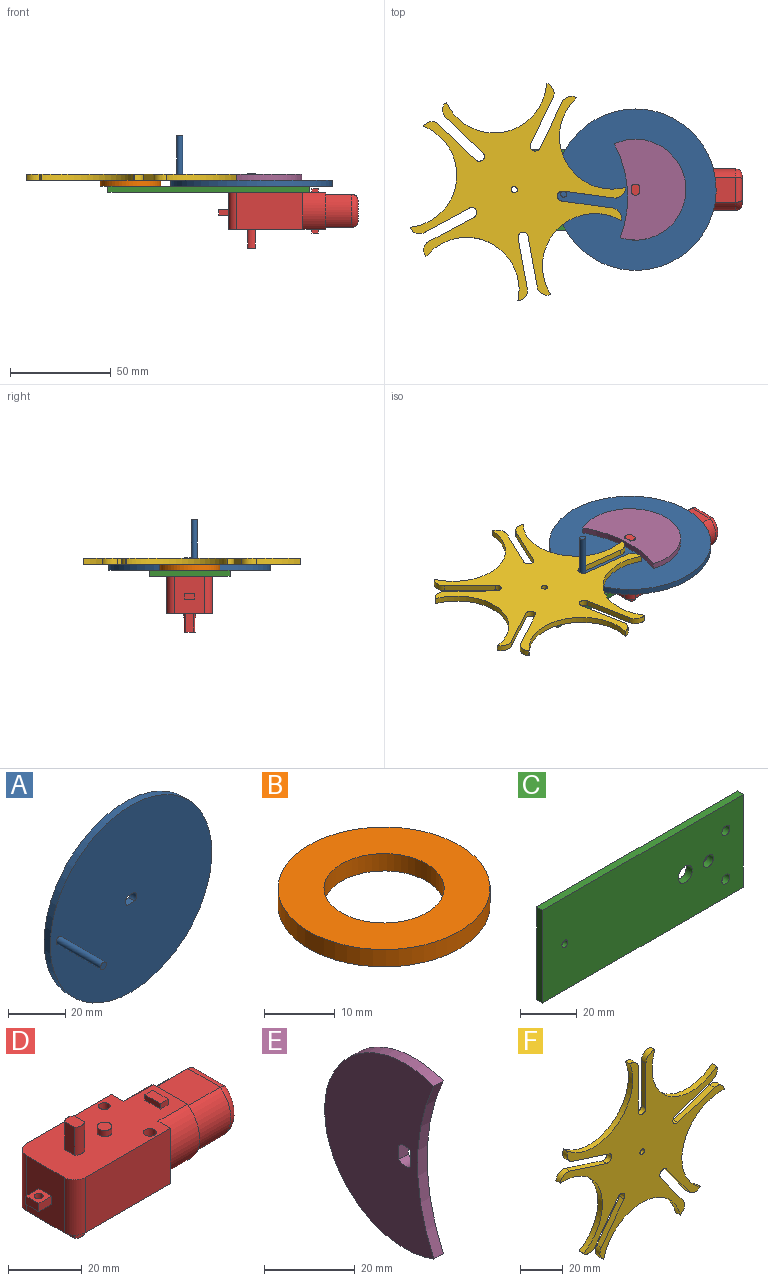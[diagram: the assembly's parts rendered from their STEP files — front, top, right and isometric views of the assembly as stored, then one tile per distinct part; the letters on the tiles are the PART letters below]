
ASSEMBLY  parts=6 mates=5
PART A: 9 faces, bbox 80x25x80 mm
  f0: cylinder r=2.7mm len=3.8mm, axis (0,1,0), area 12.6mm2, adj f1,f4,f5,f6
  f1: plane 3.84x3mm, normal (0,0,-1), area 11.5mm2, adj f0,f2,f5,f6
  f2: cylinder r=2.7mm len=3.8mm, axis (0,1,0), area 12.6mm2, adj f1,f4,f5,f6
  f3: cylinder r=40mm len=80mm, axis (0,1,0), area 754mm2, adj f5,f6
  f4: plane 3.84x3mm, normal (0,0,1), area 11.5mm2, adj f0,f2,f5,f6
  f5: plane 80x80mm, normal (0,-1,0), area 5000.8mm2, adj f0,f1,f2,f3,f4,f7
  f6: plane 80x80mm, normal (0,1,0), area 5007.9mm2, adj f0,f1,f2,f3,f4
  f7: cylinder r=1.5mm len=22mm, axis (0,1,0), area 207.3mm2, adj f5,f8
  f8: plane 3x3mm, normal (0,-1,0), area 7.1mm2, adj f7
PART B: 4 faces, bbox 30x30x3 mm
  f0: cylinder r=8.5mm len=17mm, axis (0,0,-1), area 160.2mm2, adj f2,f3
  f1: cylinder r=15mm len=30mm, axis (0,0,-1), area 282.7mm2, adj f2,f3
  f2: plane 30x30mm, normal (0,0,1), area 479.9mm2, adj f0,f1
  f3: plane 30x30mm, normal (0,0,-1), area 479.9mm2, adj f0,f1
PART C: 11 faces, bbox 100x3x40 mm
  f0: plane 100x3mm, normal (0,0,1), area 300mm2, adj f1,f8,f9,f10
  f1: plane 40x3mm, normal (-1,0,0), area 120mm2, adj f0,f2,f9,f10
  f2: plane 100x3mm, normal (0,0,-1), area 300mm2, adj f1,f8,f9,f10
  f3: cylinder r=1.5mm len=3mm, axis (0,1,0), area 28.3mm2, adj f9,f10
  f4: cylinder r=3.5mm len=7mm, axis (0,1,0), area 66mm2, adj f9,f10
  f5: cylinder r=2.5mm len=5mm, axis (0,1,0), area 47.1mm2, adj f9,f10
  f6: cylinder r=2mm len=4mm, axis (0,1,0), area 37.7mm2, adj f9,f10
  f7: cylinder r=2mm len=4mm, axis (0,1,0), area 37.7mm2, adj f9,f10
  f8: plane 40x3mm, normal (1,0,0), area 120mm2, adj f0,f2,f9,f10
  f9: plane 100x40mm, normal (0,-1,0), area 3909.7mm2, adj f0,f1,f2,f3,f4,f5,f6,f7
  f10: plane 100x40mm, normal (0,1,0), area 3909.7mm2, adj f0,f1,f2,f3,f4,f5,f6,f7
PART D: 53 faces, bbox 69.1x22.6x37 mm
  f0: plane 22.6x18.4mm, normal (1,0,0), area 66.1mm2, adj f8,f9,f17,f18,f19,f20,f21,f22
  f1: plane 9.2x4.74mm, normal (1,0,0), area 13mm2, adj f5,f8,f17
  f2: plane 9.2x4.74mm, normal (1,0,0), area 13mm2, adj f5,f9,f17
  f3: plane 9.2x4.74mm, normal (1,0,0), area 13mm2, adj f7,f9,f18
  f4: plane 18.4x14.6mm, normal (-1,0,0), area 255.1mm2, adj f8,f9,f10,f11,f12,f14,f16,f40
  f5: plane 32.8x18.4mm, normal (0,-1,0), area 603.5mm2, adj f1,f2,f8,f9,f10
  f6: plane 9.2x4.74mm, normal (1,0,0), area 13mm2, adj f7,f8,f18
  f7: plane 32.8x18.4mm, normal (0,1,0), area 603.5mm2, adj f3,f6,f8,f9,f11
  f8: plane 48.1x22.6mm, normal (0,0,1), area 906.1mm2, adj f0,f1,f4,f5,f6,f7,f10,f11
  f9: plane 48.1x22.6mm, normal (0,0,-1), area 918.6mm2, adj f0,f2,f3,f4,f5,f7,f10,f11
  f10: cylinder r=4mm len=18.4mm, axis (0,0,1), area 115.6mm2, adj f4,f5,f8,f9
  f11: cylinder r=4mm len=18.4mm, axis (0,0,-1), area 115.6mm2, adj f4,f7,f8,f9
  f12: plane 5x2.7mm, normal (0,1,0), area 13.5mm2, adj f4,f13,f16,f40
  f13: plane 5x2.7mm, normal (-1,0,0), area 13.5mm2, adj f12,f14,f16,f40
  f14: plane 5x2.7mm, normal (0,-1,0), area 13.5mm2, adj f4,f13,f16,f40
  f15: cylinder r=1.25mm len=2.7mm, axis (0,0,-1), area 21.2mm2, adj f16,f40
  f16: plane 5x5mm, normal (0,0,1), area 20.1mm2, adj f4,f12,f13,f14,f15
  f17: cylinder r=11.3mm len=18.4mm, axis (-1,0,0), area 242.9mm2, adj f0,f1,f2,f8,f9
  f18: cylinder r=11.3mm len=18.4mm, axis (-1,0,0), area 242.9mm2, adj f0,f3,f6,f8,f9
  f19: plane 13x12.47mm, normal (0,0,1), area 162.1mm2, adj f0,f20,f22,f34
  f20: cylinder r=10.3mm len=16.4mm, axis (-1,0,0), area 246.6mm2, adj f0,f19,f21,f36
  f21: plane 13x12.47mm, normal (0,0,-1), area 162.1mm2, adj f0,f20,f22,f37
  f22: cylinder r=10.3mm len=16.4mm, axis (-1,0,0), area 246.6mm2, adj f0,f19,f21,f35
  f23: plane 14.6x10.4mm, normal (1,0,0), area 137.8mm2, adj f34,f35,f36,f37
  f24: plane 5.4x3.75mm, normal (0,0,-1), area 18.5mm2, adj f25,f26,f27,f28
  f25: cylinder r=2.7mm len=9.3mm, axis (0,0,-1), area 38.6mm2, adj f9,f24,f26,f28
  f26: plane 9.3x3.89mm, normal (-1,0,0), area 36.1mm2, adj f9,f24,f25,f27
  f27: cylinder r=2.7mm len=9.3mm, axis (0,0,-1), area 38.6mm2, adj f9,f24,f26,f28
  f28: plane 9.3x3.89mm, normal (1,0,0), area 36.1mm2, adj f9,f24,f25,f27
  f29: plane 9.3x3.89mm, normal (1,0,0), area 36.1mm2, adj f8,f30,f32,f33
  f30: cylinder r=2.7mm len=9.3mm, axis (0,0,-1), area 38.6mm2, adj f8,f29,f31,f33
  f31: plane 9.3x3.89mm, normal (-1,0,0), area 36.1mm2, adj f8,f30,f32,f33
  f32: cylinder r=2.7mm len=9.3mm, axis (0,0,-1), area 38.6mm2, adj f8,f29,f31,f33
  f33: plane 5.4x3.75mm, normal (0,0,1), area 18.5mm2, adj f29,f30,f31,f32
  f34: cylinder r=3mm len=12.47mm, axis (0,1,0), area 55.1mm2, adj f19,f23,f35,f36
  f35: torus R=7.3mm, axis (1,0,0), area 76.6mm2, adj f22,f23,f34,f37
  f36: torus R=7.3mm, axis (1,0,0), area 76.6mm2, adj f20,f23,f34,f37
  f37: cylinder r=3mm len=12.47mm, axis (0,-1,0), area 55.1mm2, adj f21,f23,f35,f36
  f38: cylinder r=2mm len=4mm, axis (0,0,-1), area 25.1mm2, adj f8,f39
  f39: plane 4x4mm, normal (0,0,1), area 12.6mm2, adj f38
  f40: plane 5x5mm, normal (0,0,-1), area 20.1mm2, adj f4,f12,f13,f14,f15
  f41: cylinder r=1.78mm len=18.4mm, axis (0,0,1), area 205.7mm2, adj f8,f9
  f42: cylinder r=1.6mm len=18.4mm, axis (0,0,1), area 185mm2, adj f8,f9
  f43: plane 6x3mm, normal (0,0,-1), area 18mm2, adj f44,f45,f46,f47
  f44: plane 6x1.8mm, normal (1,0,0), area 10.8mm2, adj f9,f43,f45,f47
  f45: plane 3x1.8mm, normal (0,-1,0), area 5.4mm2, adj f9,f43,f44,f46
  f46: plane 6x1.8mm, normal (-1,0,0), area 10.8mm2, adj f9,f43,f45,f47
  f47: plane 3x1.8mm, normal (0,1,0), area 5.4mm2, adj f9,f43,f44,f46
  f48: plane 3x1.8mm, normal (0,1,0), area 5.4mm2, adj f8,f49,f51,f52
  f49: plane 6x1.8mm, normal (-1,0,0), area 10.8mm2, adj f8,f48,f50,f52
  f50: plane 3x1.8mm, normal (0,-1,0), area 5.4mm2, adj f8,f49,f51,f52
  f51: plane 6x1.8mm, normal (1,0,0), area 10.8mm2, adj f8,f48,f50,f52
  f52: plane 6x3mm, normal (0,0,1), area 18mm2, adj f48,f49,f50,f51
PART E: 8 faces, bbox 3x34x50 mm
  f0: cylinder r=56.04mm len=46.62mm, axis (-1,0,0), area 144.2mm2, adj f5,f6,f7
  f1: cylinder r=2.7mm len=3.8mm, axis (-1,0,0), area 12.6mm2, adj f2,f4,f6,f7
  f2: plane 3.84x3mm, normal (0,1,0), area 11.5mm2, adj f1,f3,f6,f7
  f3: cylinder r=2.7mm len=3.8mm, axis (-1,0,0), area 12.6mm2, adj f2,f4,f6,f7
  f4: plane 3.84x3mm, normal (0,-1,0), area 11.5mm2, adj f1,f3,f6,f7
  f5: cylinder r=25mm len=50mm, axis (-1,0,0), area 291.1mm2, adj f0,f6,f7
  f6: plane 50x34.03mm, normal (1,0,0), area 1245.4mm2, adj f0,f1,f2,f3,f4,f5
  f7: plane 50x34.03mm, normal (-1,0,0), area 1245.4mm2, adj f0,f1,f2,f3,f4,f5
PART F: 43 faces, bbox 108.5x3x103.4 mm
  f0: plane 3x0.1mm, normal (-0.51,0,-0.86), area 0.3mm2, adj f1,f39,f41,f42
  f1: cylinder r=26mm len=50.53mm, axis (0,1,0), area 207.8mm2, adj f0,f2,f41,f42
  f2: cylinder r=55mm len=3mm, axis (0,1,0), area 0.6mm2, adj f1,f3,f41,f42
  f3: cylinder r=5mm len=7.38mm, axis (0,1,0), area 25.8mm2, adj f2,f4,f41,f42
  f4: plane 20.58x14.95mm, normal (0.81,0,0.59), area 76.3mm2, adj f3,f5,f41,f42
  f5: cylinder r=2.5mm len=4.52mm, axis (0,1,0), area 23.6mm2, adj f4,f6,f41,f42
  f6: plane 20.58x14.95mm, normal (-0.81,0,-0.59), area 76.3mm2, adj f5,f7,f41,f42
  f7: cylinder r=5mm len=7.36mm, axis (0,1,0), area 25mm2, adj f6,f8,f41,f42
  f8: plane 3x0.09mm, normal (0.66,0,-0.75), area 0.3mm2, adj f7,f9,f41,f42
  f9: cylinder r=26mm len=48.08mm, axis (0,1,0), area 207.8mm2, adj f8,f10,f41,f42
  f10: cylinder r=55mm len=3mm, axis (0,1,0), area 0.6mm2, adj f9,f11,f41,f42
  f11: cylinder r=5mm len=6.48mm, axis (0,1,0), area 25.8mm2, adj f10,f12,f41,f42
  f12: plane 24.19x7.86mm, normal (-0.31,0,0.95), area 76.3mm2, adj f11,f13,f41,f42
  f13: cylinder r=2.5mm len=4.88mm, axis (0,1,0), area 23.6mm2, adj f12,f14,f41,f42
  f14: plane 24.19x7.86mm, normal (0.31,0,-0.95), area 76.3mm2, adj f13,f15,f41,f42
  f15: cylinder r=5mm len=6.75mm, axis (0,1,0), area 25mm2, adj f14,f16,f41,f42
  f16: plane 3x0.11mm, normal (0.92,0,0.4), area 0.3mm2, adj f15,f17,f41,f42
  f17: cylinder r=26mm len=42.76mm, axis (0,1,0), area 207.8mm2, adj f16,f18,f41,f42
  f18: cylinder r=55mm len=3mm, axis (0,1,0), area 0.6mm2, adj f17,f19,f41,f42
  f19: cylinder r=5mm len=5.75mm, axis (0,1,0), area 25.8mm2, adj f18,f20,f41,f42
  f20: plane 25.43x3mm, normal (-1,0,0), area 76.3mm2, adj f19,f21,f41,f42
  f21: cylinder r=2.5mm len=5mm, axis (0,1,0), area 23.6mm2, adj f20,f22,f41,f42
  f22: plane 25.44x3mm, normal (1,0,0), area 76.3mm2, adj f21,f23,f41,f42
  f23: cylinder r=5mm len=5.48mm, axis (0,1,0), area 25mm2, adj f22,f24,f41,f42
  f24: plane 3x0.12mm, normal (-0.1,0,1), area 0.3mm2, adj f23,f25,f41,f42
  f25: cylinder r=26mm len=42.89mm, axis (0,1,0), area 207.8mm2, adj f24,f26,f41,f42
  f26: cylinder r=55mm len=3mm, axis (0,1,0), area 0.6mm2, adj f25,f27,f41,f42
  f27: cylinder r=5mm len=7mm, axis (0,1,0), area 25.8mm2, adj f26,f28,f41,f42
  f28: plane 24.19x7.86mm, normal (-0.31,0,-0.95), area 76.3mm2, adj f27,f29,f41,f42
  f29: cylinder r=2.5mm len=4.88mm, axis (0,1,0), area 23.6mm2, adj f28,f30,f41,f42
  f30: plane 24.19x7.86mm, normal (0.31,0,0.95), area 76.3mm2, adj f29,f31,f41,f42
  f31: cylinder r=5mm len=6.43mm, axis (0,1,0), area 25mm2, adj f30,f32,f41,f42
  f32: plane 3x0.11mm, normal (-0.98,0,0.22), area 0.3mm2, adj f31,f33,f41,f42
  f33: cylinder r=26mm len=48.17mm, axis (0,1,0), area 207.8mm2, adj f32,f34,f41,f42
  f34: cylinder r=55mm len=3mm, axis (0,1,0), area 0.6mm2, adj f33,f35,f41,f42
  f35: cylinder r=5mm len=7.56mm, axis (0,1,0), area 25.8mm2, adj f34,f36,f41,f42
  f36: plane 20.58x14.95mm, normal (0.81,0,-0.59), area 76.3mm2, adj f35,f37,f41,f42
  f37: cylinder r=2.5mm len=4.52mm, axis (0,1,0), area 23.6mm2, adj f36,f38,f41,f42
  f38: plane 20.58x14.95mm, normal (-0.81,0,0.59), area 76.3mm2, adj f37,f39,f41,f42
  f39: cylinder r=5mm len=7.25mm, axis (0,1,0), area 25mm2, adj f0,f38,f41,f42
  f40: cylinder r=1.5mm len=3mm, axis (0,1,0), area 28.3mm2, adj f41,f42
  f41: plane 108.54x103.37mm, normal (0,-1,0), area 3829.3mm2, adj f0,f1,f2,f3,f4,f5,f6,f7
  f42: plane 108.54x103.37mm, normal (0,1,0), area 3829.3mm2, adj f0,f1,f2,f3,f4,f5,f6,f7
PLACE A rot(axis=(-1,-0.03,0.03),90.1deg) t=(-17.24,-4.71,4.26)mm
PLACE B rot(axis=(1,0,0),180deg) t=(-77.24,-4.71,7.26)mm
PLACE C rot(axis=(1,0,0),90deg) t=(-38.34,-4.71,4.26)mm
PLACE D t=(-28.54,-4.71,-7.94)mm fixed
PLACE E rot(axis=(0.56,0.6,-0.56),117.9deg) t=(-17.24,-4.71,10.26)mm
PLACE F rot(axis=(0.29,-0.68,-0.68),147.7deg) t=(-77.24,-4.71,10.26)mm
MATE revolute B.f1 <-> C.f3  axis (0,0,-1) through (-77.24,-4.71,4.26)mm
MATE revolute B.f1 <-> F.f40  axis (0,0,1) through (-77.24,-4.71,7.26)mm
MATE fastened E.f5 <-> A.f2  axis (0,0,-1) through (-17.24,-4.71,7.26)mm
MATE revolute A.f0 <-> C.f4  axis (0,0,-1) through (-17.24,-4.71,4.26)mm
MATE fastened C.f4 <-> D.f25  axis (0,0,-1) through (-17.24,-4.71,1.26)mm
